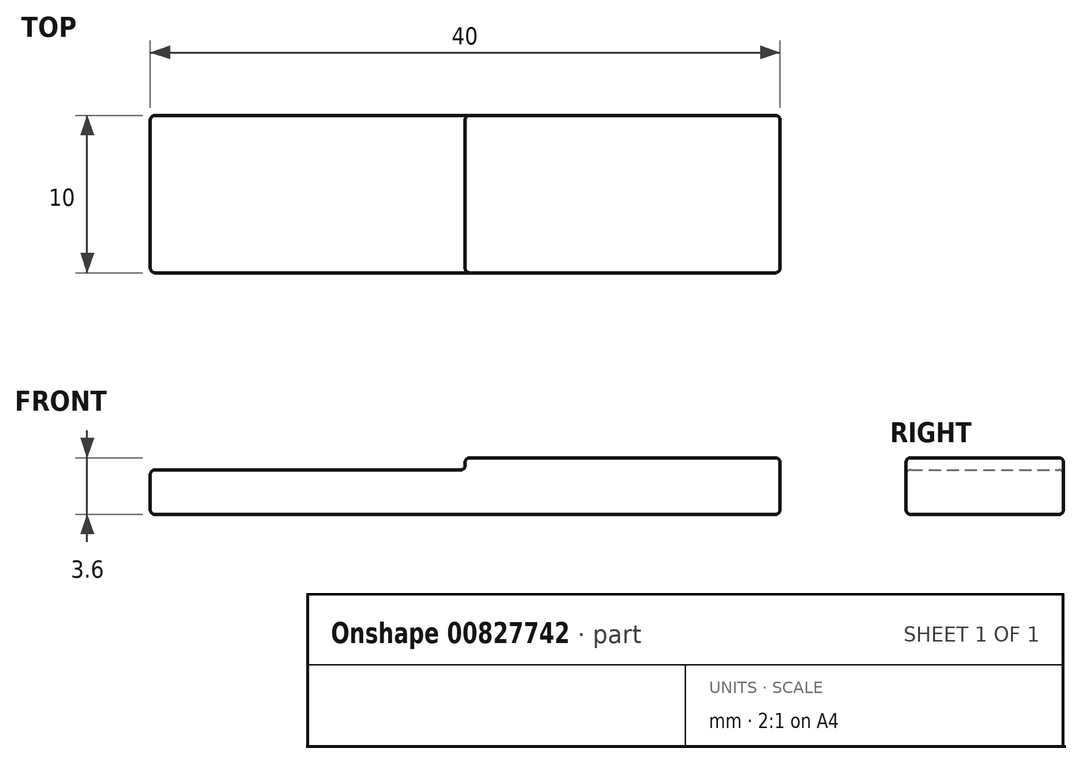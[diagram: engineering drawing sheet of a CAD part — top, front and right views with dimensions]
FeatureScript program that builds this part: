
annotation { "Feature Type Name" : "Feature", "Feature Type Description" : "" }
export const myFeature = defineFeature(function(context is Context, id is Id, definition is map)
    precondition{}
    {
        {
            var Q0;
            Q0=qCreatedBy(makeId("Front.planeOp"),FACE);
            var sketch = newSketch(context, id + "F0", { "sketchPlane" : qUnion([Q0])});
            skLineSegment(sketch, "E0", {"start": v(0, 0) * mm, "end": v(40, 0) * mm});
            skLineSegment(sketch, "E1", {"start": v(40, 0) * mm, "end": v(40, 3.6) * mm});
            skLineSegment(sketch, "E2", {"start": v(40, 3.6) * mm, "end": v(20, 3.6) * mm});
            skLineSegment(sketch, "E3", {"start": v(20, 3.6) * mm, "end": v(20, 2.83) * mm});
            skLineSegment(sketch, "E4", {"start": v(20, 2.83) * mm, "end": v(0, 2.83) * mm});
            skLineSegment(sketch, "E5", {"start": v(0, 2.83) * mm, "end": v(0, 0) * mm});
            skSolve(sketch);
        }
        {
            var Q0;
            Q0=makeQuery(id+"F0.imprint","IMPRINT",FACE,{"disambiguationData":[TD([[makeQuery(id+"F0.imprint","IMPRINT",EDGE,{"derivedFrom":sQuery(id+"F0.wireOp",EDGE,"E0")}),1.0]])]});
            extrude(context, id + "F1", {"entities" : qUnion([Q0]), "endBound" : BoundingType.SYMMETRIC, "depth" : 10 * mm, "offsetDistance" : 25.4 * mm});
        }
        {
            var Q0;
            Q0=makeQuery(id+"F1.opExtrude","CAP_EDGE",EDGE,{"disambiguationData":[OSD([sQuery(id+"F0.wireOp",EDGE,"E4")])],"isStart":true});
            var Q1;
            Q1=makeQuery(id+"F1.opExtrude","SWEPT_EDGE",EDGE,{"disambiguationData":[OSD([sQuery(id+"F0.wireOp",EDGE,"E4"),sQuery(id+"F0.wireOp",EDGE,"E5")])]});
            var Q2;
            Q2=makeQuery(id+"F1.opExtrude","CAP_EDGE",EDGE,{"disambiguationData":[OSD([sQuery(id+"F0.wireOp",EDGE,"E5")])],"isStart":true});
            var Q3;
            Q3=makeQuery(id+"F1.opExtrude","CAP_EDGE",EDGE,{"disambiguationData":[OSD([sQuery(id+"F0.wireOp",EDGE,"E5")])],"isStart":false});
            var Q4;
            Q4=makeQuery(id+"F1.opExtrude","SWEPT_EDGE",EDGE,{"disambiguationData":[OSD([sQuery(id+"F0.wireOp",EDGE,"E0"),sQuery(id+"F0.wireOp",EDGE,"E5")])]});
            var Q5;
            Q5=makeQuery(id+"F1.opExtrude","CAP_EDGE",EDGE,{"disambiguationData":[OSD([sQuery(id+"F0.wireOp",EDGE,"E0")])],"isStart":false});
            var Q6;
            Q6=makeQuery(id+"F1.opExtrude","CAP_EDGE",EDGE,{"disambiguationData":[OSD([sQuery(id+"F0.wireOp",EDGE,"E4")])],"isStart":false});
            var Q7;
            Q7=makeQuery(id+"F1.opExtrude","SWEPT_EDGE",EDGE,{"disambiguationData":[OSD([sQuery(id+"F0.wireOp",EDGE,"E3"),sQuery(id+"F0.wireOp",EDGE,"E4")])]});
            var Q8;
            Q8=makeQuery(id+"F1.opExtrude","CAP_EDGE",EDGE,{"disambiguationData":[OSD([sQuery(id+"F0.wireOp",EDGE,"E3")])],"isStart":true});
            var Q9;
            Q9=makeQuery(id+"F1.opExtrude","CAP_EDGE",EDGE,{"disambiguationData":[OSD([sQuery(id+"F0.wireOp",EDGE,"E3")])],"isStart":false});
            var Q10;
            Q10=makeQuery(id+"F1.opExtrude","SWEPT_EDGE",EDGE,{"disambiguationData":[OSD([sQuery(id+"F0.wireOp",EDGE,"E2"),sQuery(id+"F0.wireOp",EDGE,"E3")])]});
            var Q11;
            Q11=makeQuery(id+"F1.opExtrude","CAP_EDGE",EDGE,{"disambiguationData":[OSD([sQuery(id+"F0.wireOp",EDGE,"E2")])],"isStart":false});
            var Q12;
            Q12=makeQuery(id+"F1.opExtrude","CAP_EDGE",EDGE,{"disambiguationData":[OSD([sQuery(id+"F0.wireOp",EDGE,"E2")])],"isStart":true});
            var Q13;
            Q13=makeQuery(id+"F1.opExtrude","SWEPT_EDGE",EDGE,{"disambiguationData":[OSD([sQuery(id+"F0.wireOp",EDGE,"E1"),sQuery(id+"F0.wireOp",EDGE,"E2")])]});
            var Q14;
            Q14=makeQuery(id+"F1.opExtrude","CAP_EDGE",EDGE,{"disambiguationData":[OSD([sQuery(id+"F0.wireOp",EDGE,"E1")])],"isStart":false});
            var Q15;
            Q15=makeQuery(id+"F1.opExtrude","CAP_EDGE",EDGE,{"disambiguationData":[OSD([sQuery(id+"F0.wireOp",EDGE,"E1")])],"isStart":true});
            var Q16;
            Q16=makeQuery(id+"F1.opExtrude","SWEPT_EDGE",EDGE,{"disambiguationData":[OSD([sQuery(id+"F0.wireOp",EDGE,"E0"),sQuery(id+"F0.wireOp",EDGE,"E1")])]});
            var Q17;
            Q17=makeQuery(id+"F1.opExtrude","CAP_EDGE",EDGE,{"disambiguationData":[OSD([sQuery(id+"F0.wireOp",EDGE,"E0")])],"isStart":true});
            fillet(context, id + "F2", {"entities" : qUnion([Q0, Q1, Q2, Q3, Q4, Q5, Q6, Q7, Q8, Q9, Q10, Q11, Q12, Q13, Q14, Q15, Q16, Q17]), "radius" : .3 * mm, "tangentPropagation" : true, "allowEdgeOverflow" : false});
        }
    });
